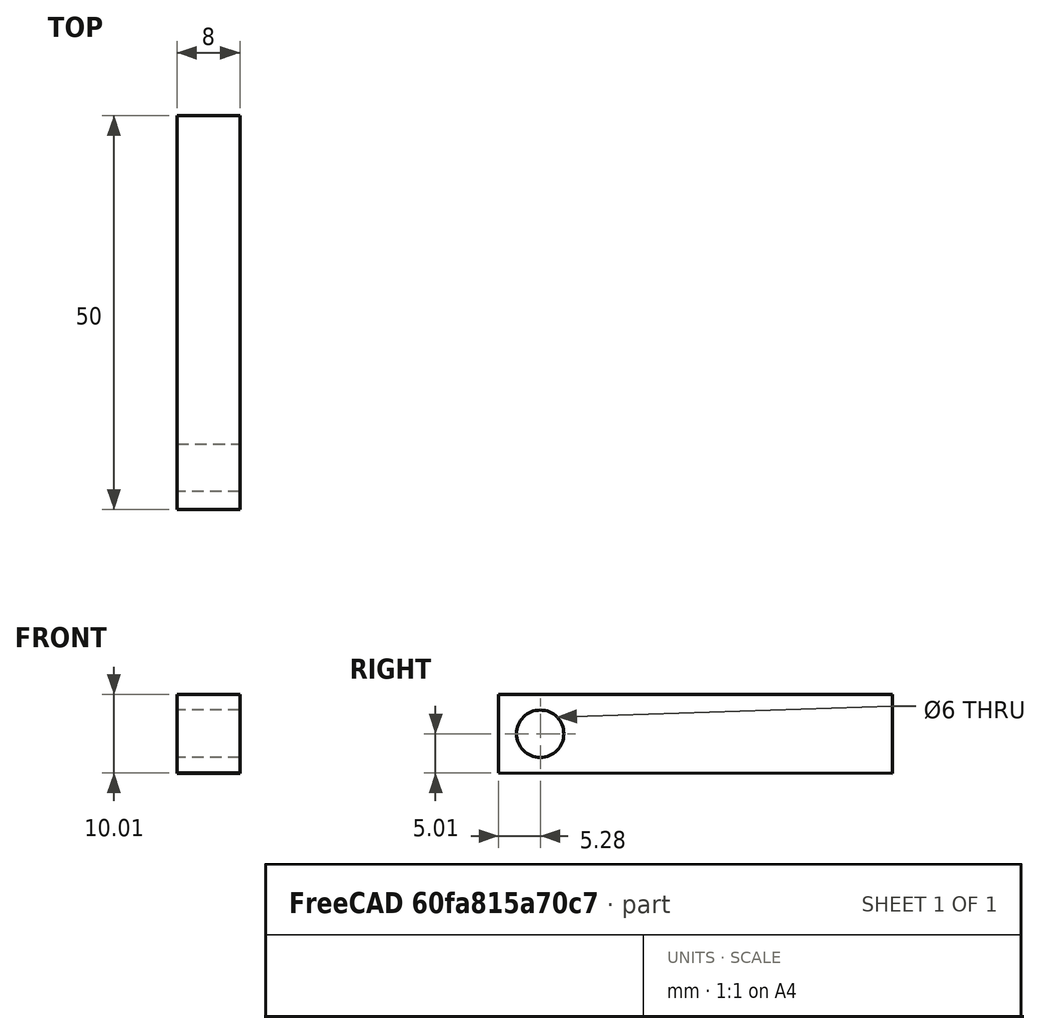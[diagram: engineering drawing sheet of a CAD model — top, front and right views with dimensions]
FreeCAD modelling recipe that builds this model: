
FCSTD DOCUMENT  (FreeCAD 0.21R33668 +26 (Git))
Label: Piece_000
License: All rights reserved
LicenseURL: http://en.wikipedia.org/wiki/All_rights_reserved
objects: PartDesign::CoordinateSystem×1, Sketcher::SketchObject×1, PartDesign::Pad×1, PartDesign::Body×1
note: 5 computed .brp shape members not serialized (recipe doc carries the construction recipe); baked Part::Feature solids carry a one-line shape summary decoded from their .brp

FEATURE [PartDesign::CoordinateSystem] LCS_0
  AttacherType = Attacher::AttachEngine3D
  MapMode = 2
  Support = -> [X_Axis]
FEATURE [Sketcher::SketchObject] Sketch
  FullyConstrained = false
  MapMode = 5
  Placement = pos=(0,0,0) rot=(0.57735,0.57735,0.57735;2.0944rad)
  Support = -> [YZ_Plane]
  sketch-geometry (5):
    g0: LineSegment StartX=-5.27726 StartY=5.00146 StartZ=0 EndX=44.7227 EndY=4.98767 EndZ=0
    g1: LineSegment StartX=44.7227 StartY=4.98767 StartZ=0 EndX=44.72 EndY=-5.01233 EndZ=0
    g2: LineSegment StartX=44.72 StartY=-5.01233 StartZ=0 EndX=-5.28002 EndY=-4.99854 EndZ=0
    g3: LineSegment StartX=-5.28002 StartY=-4.99854 StartZ=0 EndX=-5.27726 EndY=5.00146 EndZ=0
    g4: Circle CenterX=0 CenterY=0 CenterZ=0 NormalX=0 NormalY=0 NormalZ=1 AngleXU=0 Radius=3
  constraints (13):
    c: Coincident(g0,g1)
    c: Coincident(g1,g2)
    c: Coincident(g2,g3)
    c: Coincident(g3,g0)
    c: Distance(g0,g2) = 10
    c: Distance(g0,g0) = 50
    c: Parallel(g0,g2)
    c: Parallel(g3,g1)
    c: Perpendicular(g0,g1)
    c: Coincident(g4,g-1)
    c: Radius(g4) = 3
    c: Distance(g4,g0) = 45
    c: Distance(g4,g1) = 45
FEATURE [PartDesign::Pad] Pad
  Direction = (1,-2e-16,3e-16)
  Length = 8
  Length2 = 10
  Placement = pos=(0,0,0) rot=(1,1,1;2.0944rad)
  Profile = -> Sketch
  ReferenceAxis = -> Sketch [N_Axis]
  Type = 0
FEATURE [PartDesign::Body] Body
  Group = -> [LCS_0,Sketch,Pad]
  Origin = -> Origin
  Tip = -> Pad
